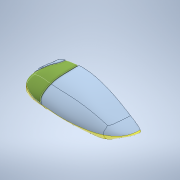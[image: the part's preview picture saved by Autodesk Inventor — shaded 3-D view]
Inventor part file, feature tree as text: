
AUTODESK INVENTOR PART (.ipt)
format: ipt  version: 2021 (Build 250183000, 183)  size: 4,152,320 bytes
history: native  units: mm
features: other x27, sketch x23, extrude x14, split x10, plane x7, surface_op x7, fillet x2, thicken_offset x2, shell x1, sweep x1, hole x1
ambient origin geometry x8: Origin, YZ Plane, XZ Plane, XY Plane, X Axis, Y Axis, Z Axis, Center Point
bodies: Solid2 (feature_tree), Solid3 (feature_tree), Solid4 (feature_tree), Solid5 (feature_tree), Solid6 (feature_tree)
feature tree (95):
  other  "CrossSection1"
  other  "Curvature1"
  sketch  "Sketch1"  dims[d1=120.0mm d5=60.0mm d6=7.0mm d9=120.0mm]
  sketch  "Sketch2"  dims[d13=42.0mm d14=60.0mm]
  other  "Form2"
  extrude  "Extrusion5"  Depth=60.0mm
  sketch  "Sketch9"  dims[d44=48.0mm d45=0.0mm d46=8.0mm]
  sketch  "3D Sketch1"
  split  "Split1"
  split  "Split2"
  plane  "Work Plane1"
  split  "Split3"
  other  "Ruled Surface1"
  surface_op  "Extend1"
  other  "Ruled Surface6"
  surface_op  "Extend2"
  other  "Ruled Surface7"
  surface_op  "Extend3"
  surface_op  "Stitch Surface1"
  other  "Ruled Surface8"
  surface_op  "Extend4"
  surface_op  "Stitch Surface2"
  split  "Split4"
  shell  "Shell1"  Thickness=7.0mm
  split  "Split5"
  surface_op  "Extend5"
  split  "Split6"
  split  "Split7"
  split  "Split8"
  fillet  "Fillet1"  Radius=120.0mm
  plane  "Work Plane2"
  plane  "Work Plane3"
  split  "Split9"
  split  "Split10"
  sweep  "Sweep1"
  extrude  "Extrusion6"  Depth=1.0mm
  extrude  "Extrusion7"  Depth=8.0mm
  extrude  "Extrusion8"  Depth=3.0mm
  thicken_offset  "Thicken1"
  thicken_offset  "Thicken2"
  extrude  "Extrusion9"  Depth=3.0mm
  fillet  "Fillet2"  Radius=10.0mm
  hole  "Hole1"  [1 undecoded]
  plane  "Work Plane4"
  extrude  "Extrusion10"  Depth=10.0mm TaperAngle=0.0deg
  extrude  "Extrusion11"  Depth=1.3mm
  extrude  "Extrusion12"  Depth=1.3mm
  other  "Snap Fit1"
  plane  "Work Plane5"
  plane  "Work Plane6"
  other  "Lip1"
  other  "Lip2"
  sketch  "Sketch22"  dims[d90=1.0mm]
  other  "Boss1"
  other  "Boss2"
  extrude  "Extrusion13"  Depth=1.0mm
  plane  "Work Plane7"
  extrude  "Extrusion14"  Depth=1.0mm
  extrude  "Extrusion15"  Depth=1.0mm
  extrude  "Extrusion16"  Depth=14.0mm
  other  "Image1"
  other  "Image2"
  sketch  "Sketch8"  dims[d25=0.5mm d26=2.0mm d27=0.0mm d28=20.0mm d41=1.0mm]
  other  "Project to Surface1"
  other  "Srf1"
  other  "Srf2"
  other  "Srf7"
  other  "Srf8"
  other  "Srf9"
  other  "Srf10"
  other  "Srf11"
  other  "Srf12"
  sketch  "Sketch10"  dims[d47=3.0mm d48=3.0mm]
  other  "Srf13"
  sketch  "Sketch11"  dims[d49=10.0mm d50=0.0mm d51=3.0mm d62=10.0mm d63=0.0mm]
  other  "Srf14"
  sketch  "3D Sketch2"
  sketch  "Sketch12"  dims[d64=3.0mm d65=10.0mm d66=0.0mm]
  sketch  "Sketch13"  dims[d67=3.0mm d68=10.0mm d69=0.0mm]
  sketch  "Sketch14"  dims[d70=3.0mm d71=1.3mm]
  sketch  "Sketch15"  dims[d72=1.3mm d73=1.3mm]
  sketch  "Sketch16"  dims[d74=4.0mm d75=1.0mm]
  sketch  "Sketch17"  dims[d76=100.0mm d77=0.0mm d78=1.0mm]
  sketch  "Sketch18"  dims[d79=40.0mm d80=0.0mm d81=1.0mm]
  sketch  "Sketch19"  dims[d82=14.0mm d83=-14.0mm d84=14.0mm]
  sketch  "Sketch20"  dims[d85=1.3mm d86=0.0mm d87=0.0mm]
  sketch  "Sketch21"  dims[d88=2.3mm d89=20.0mm]
  sketch  "Sketch23"  dims[d91=1.0mm]
  sketch  "Sketch24"  dims[d92=25.0mm d93=0.0mm]
  sketch  "Sketch25"  dims[d94=20.0mm]
  sketch  "Sketch26"  dims[d95=6.0mm d96=5.0mm d97=3.0mm d98=1.3mm d99=0.0mm d100=30.0mm d101=1.0mm d102=0.5mm d103=15.0mm d104=0.0mm d105=0.0mm d106=1.0mm d107=1.0mm d108=1.0mm d109=1.0mm d110=48.0mm d111=30.0mm d112=27.0mm d113=8.0mm d114=-4.363323mm d115=4.0mm d116=9.0mm d117=9.0mm d118=4.0mm d119=4.0mm d120=2.0mm d121=2.0mm d122=4.0mm d123=2.0mm d124=90.0deg d125=100.0mm d126=20.594885mm d127=0.0mm d128=2.5mm d129=2.5mm d130=8.0mm d131=0.0mm d132=1.5mm d133=1.5mm d134=1.5mm d135=0.0mm d136=20.0mm d137=1.3mm d138=4.0mm d139=7.0mm d140=1.5mm d141=0.0mm d142=10.0mm d143=7.0mm d144=1.35mm d145=1.2mm d146=0.7mm d147=0.7mm d148=3.0mm d149=3.0mm d150=0.5mm d151=0.5mm d152=12.217305mm d153=3.490659mm d154=35.0mm d155=-4.0mm d156=1.0mm d157=0.65mm d158=0.0mm d159=0.0mm d160=0.0mm d161=0.0mm d162=1.0mm d163=0.65mm d164=0.0mm d165=0.0mm d166=0.0mm d167=0.0mm d168=18.0mm d169=36.0mm d170=50.0mm d171=40.0mm d172=50.0mm d173=0.3mm d174=0.0mm d175=4.0mm d176=1.3mm d177=0.5mm d178=3.0mm d179=1.25mm d180=2.2mm d181=0.0mm d182=0.0mm d183=0.0mm d184=0.0mm d185=90.0deg d186=20.0mm d188=2.0mm d189=2.0mm d190=10.0mm d191=0.0mm d192=1.745329mm d193=0.436332mm d194=0.0mm d195=0.0mm d196=0.0mm d197=360.0deg d198=0.5mm d199=0.0mm d200=3.0mm d201=1.0mm d202=9.5mm d203=0.174533mm d204=0.174533mm d205=20.0mm d207=2.0mm d208=2.0mm d209=10.0mm d210=0.0mm d211=1.745329mm d212=0.436332mm d213=0.0mm d214=0.0mm d215=0.0mm d216=360.0deg d217=0.8mm d218=6.0mm d219=1.0mm d220=1.0mm d221=6.0mm d222=0.0mm d223=0.0mm d224=-12.0mm d225=2.0mm d226=2.0mm d227=3.0mm d228=39.0mm d229=3.0mm d230=39.0mm d231=0.0mm d232=0.0mm d233=1.2mm d234=3.4mm d235=1.3mm d236=0.0mm d237=0.0mm d238=4.0mm d239=4.0mm d240=0.0mm d241=0.0mm d30=0.5mm d31=0.872665mm d32=0.5mm d33=0.872665mm d34=0.872665mm d42=0.5mm d43=0.872665mm]
  other  "OffsetSrf1"
  other  "OffsetSrf2"
  extrude  "ExtrusionSrf1"  TaperAngle=0.0deg  [1 undecoded]
  extrude  "ExtrusionSrf2"  Depth=20.0mm
note: 2 required parameter values undecoded (feature->parameter linkage not recoverable at this tier; creation-order binding heuristic only, values carry confidence <= 0.55)
